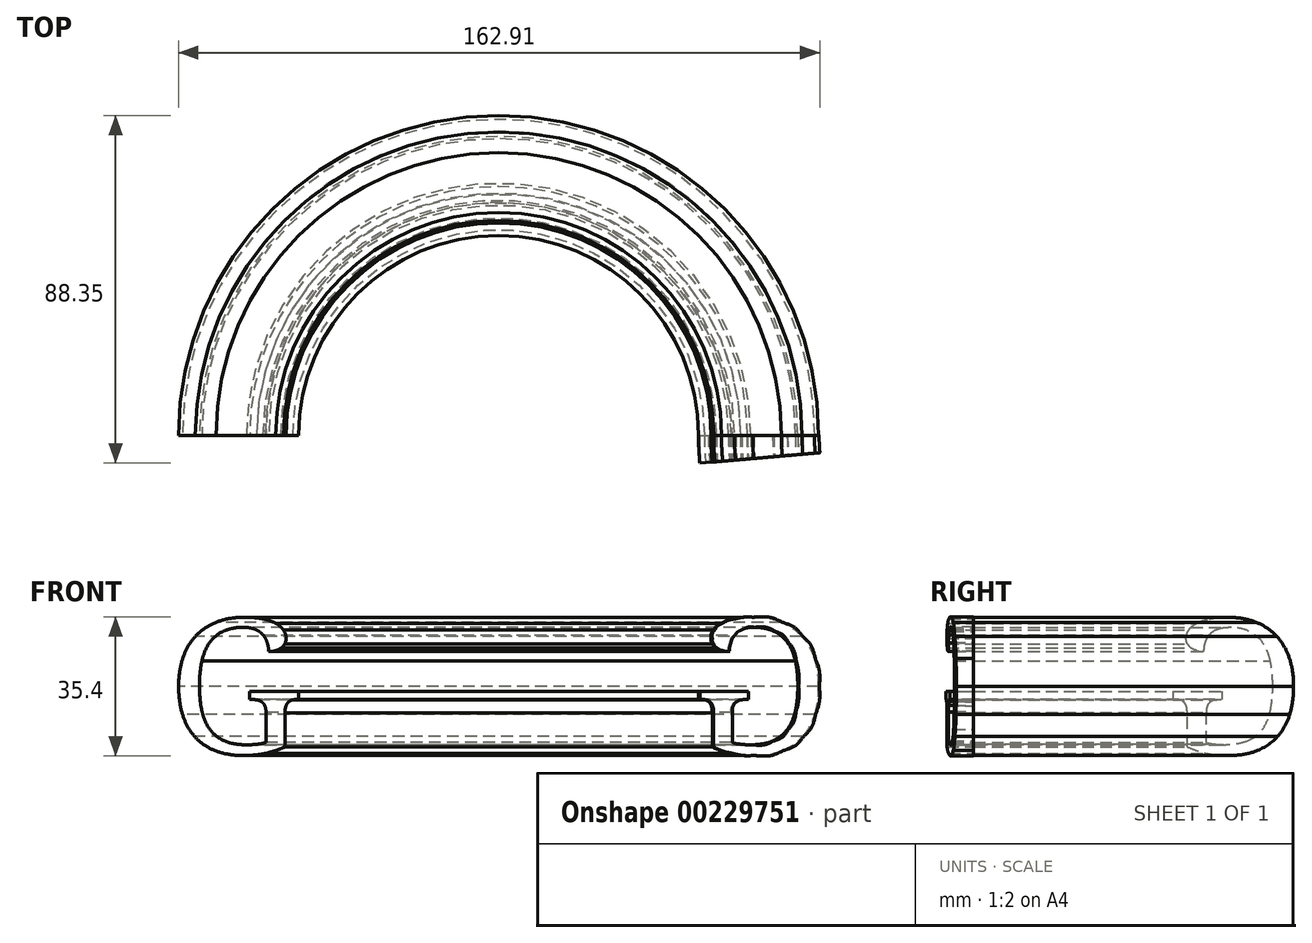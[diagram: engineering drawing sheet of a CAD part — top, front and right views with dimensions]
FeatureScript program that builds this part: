
annotation { "Feature Type Name" : "Feature", "Feature Type Description" : "" }
export const myFeature = defineFeature(function(context is Context, id is Id, definition is map)
    precondition{}
    {
        {
            var Q0;
            Q0=qCreatedBy(makeId("Front.planeOp"),FACE);
            var sketch = newSketch(context, id + "F0", { "sketchPlane" : qUnion([Q0])});
            skLineSegment(sketch, "E0", {"start": v(0, 68.36) * mm, "end": v(0, -21.66) * mm, "construction": true});
            skText(sketch, "E1", { "text": "G", "fontName": "NotoSerif-Regular.ttf"});
            const initialGuessF0  = {"E1": [-0.08404, 0.0145, 1, 0, 0.03445]};
            skSetInitialGuess(sketch, initialGuessF0);
            skSolve(sketch);
        }
        {
            var Q0;
            Q0 = qSketchRegion(id + "F0", true);
            var Q1;
            Q1=sQuery(id+"F0.wireOp",EDGE,"E0");
            revolve(context, id + "F1", {"entities" : qUnion([Q0]), "axis" : qUnion([Q1]), "revolveType" : RevolveType.ONE_DIRECTION, "angle" : 180 * degree});
        }
        {
            var Q0;
            Q0=makeQuery(id+"F1.opRevolve","CAP_FACE",FACE,{"disambiguationData":[OSD([sQuery(id+"F0.wireOp",EDGE,"E1.sketch_text.stroke-0"),sQuery(id+"F0.wireOp",EDGE,"E1.sketch_text.stroke-1"),sQuery(id+"F0.wireOp",EDGE,"E1.sketch_text.stroke-2"),sQuery(id+"F0.wireOp",EDGE,"E1.sketch_text.stroke-3"),sQuery(id+"F0.wireOp",EDGE,"E1.sketch_text.stroke-4"),sQuery(id+"F0.wireOp",EDGE,"E1.sketch_text.stroke-5"),sQuery(id+"F0.wireOp",EDGE,"E1.sketch_text.stroke-6"),sQuery(id+"F0.wireOp",EDGE,"E1.sketch_text.stroke-7"),sQuery(id+"F0.wireOp",EDGE,"E1.sketch_text.stroke-8"),sQuery(id+"F0.wireOp",EDGE,"E1.sketch_text.stroke-9"),sQuery(id+"F0.wireOp",EDGE,"E1.sketch_text.stroke-10"),sQuery(id+"F0.wireOp",EDGE,"E1.sketch_text.stroke-11"),sQuery(id+"F0.wireOp",EDGE,"E1.sketch_text.stroke-12"),sQuery(id+"F0.wireOp",EDGE,"E1.sketch_text.stroke-13"),sQuery(id+"F0.wireOp",EDGE,"E1.sketch_text.stroke-14"),sQuery(id+"F0.wireOp",EDGE,"E1.sketch_text.stroke-15"),sQuery(id+"F0.wireOp",EDGE,"E1.sketch_text.stroke-16"),sQuery(id+"F0.wireOp",EDGE,"E1.sketch_text.stroke-17"),sQuery(id+"F0.wireOp",EDGE,"E1.sketch_text.stroke-18"),sQuery(id+"F0.wireOp",EDGE,"E1.sketch_text.stroke-19"),sQuery(id+"F0.wireOp",EDGE,"E1.sketch_text.stroke-20"),sQuery(id+"F0.wireOp",EDGE,"E1.sketch_text.stroke-21"),sQuery(id+"F0.wireOp",EDGE,"E1.sketch_text.stroke-22"),sQuery(id+"F0.wireOp",EDGE,"E1.sketch_text.stroke-23"),sQuery(id+"F0.wireOp",EDGE,"E1.sketch_text.stroke-24"),sQuery(id+"F0.wireOp",EDGE,"E1.sketch_text.stroke-25"),sQuery(id+"F0.wireOp",EDGE,"E1.sketch_text.stroke-26"),sQuery(id+"F0.wireOp",EDGE,"E1.sketch_text.stroke-27"),sQuery(id+"F0.wireOp",EDGE,"E1.sketch_text.stroke-28"),sQuery(id+"F0.wireOp",EDGE,"E1.sketch_text.stroke-29"),sQuery(id+"F0.wireOp",EDGE,"E1.sketch_text.stroke-30"),sQuery(id+"F0.wireOp",EDGE,"E1.sketch_text.stroke-31"),sQuery(id+"F0.wireOp",EDGE,"E1.sketch_text.stroke-32"),sQuery(id+"F0.wireOp",EDGE,"E1.sketch_text.stroke-33"),sQuery(id+"F0.wireOp",EDGE,"E1.sketch_text.stroke-34"),sQuery(id+"F0.wireOp",EDGE,"E1.sketch_text.stroke-35"),sQuery(id+"F0.wireOp",EDGE,"E1.sketch_text.stroke-36"),sQuery(id+"F0.wireOp",EDGE,"E1.sketch_text.stroke-37"),sQuery(id+"F0.wireOp",EDGE,"E1.sketch_text.stroke-38"),sQuery(id+"F0.wireOp",EDGE,"E1.sketch_text.stroke-39"),sQuery(id+"F0.wireOp",EDGE,"E1.sketch_text.stroke-40"),sQuery(id+"F0.wireOp",EDGE,"E1.sketch_text.stroke-41"),sQuery(id+"F0.wireOp",EDGE,"E1.sketch_text.stroke-42"),sQuery(id+"F0.wireOp",EDGE,"E1.sketch_text.stroke-43"),sQuery(id+"F0.wireOp",EDGE,"E1.sketch_text.stroke-44"),sQuery(id+"F0.wireOp",EDGE,"E1.sketch_text.stroke-45"),sQuery(id+"F0.wireOp",EDGE,"E1.sketch_text.stroke-46")])],"isStart":false});
            cPlane(context, id + "F2", {"entities" : qUnion([Q0]), "cplaneType" : CPlaneType.OFFSET, "offset" : 0 * mm, "width" : 152.4 * mm, "height" : 152.4 * mm});
        }
        {
            var Q0;
            Q0=qCreatedBy(id+"F2.planeOp",FACE);
            var sketch = newSketch(context, id + "F3", { "sketchPlane" : qUnion([Q0])});
            skFitSpline(sketch, "E2.0.0", {"points": [v(59.23, 14.57) * mm, v(61.78, 14.04) * mm, v(64.86, 14.04) * mm]});
            skFitSpline(sketch, "E2.0.1", {"points": [v(64.86, 14.04) * mm, v(69.02, 14.04) * mm, v(72.11, 15.3) * mm]});
            skFitSpline(sketch, "E2.0.2", {"points": [v(72.11, 15.3) * mm, v(75.2, 16.56) * mm, v(77.25, 18.88) * mm]});
            skFitSpline(sketch, "E2.0.3", {"points": [v(77.25, 18.88) * mm, v(79.3, 21.19) * mm, v(80.3, 24.44) * mm]});
            skFitSpline(sketch, "E2.0.4", {"points": [v(80.3, 24.44) * mm, v(81.3, 27.69) * mm, v(81.3, 31.63) * mm]});
            skFitSpline(sketch, "E2.0.5", {"points": [v(81.3, 31.63) * mm, v(81.3, 35.5) * mm, v(80.24, 38.73) * mm]});
            skFitSpline(sketch, "E2.0.6", {"points": [v(80.24, 38.73) * mm, v(79.18, 41.96) * mm, v(77.06, 44.27) * mm]});
            skFitSpline(sketch, "E2.0.7", {"points": [v(77.06, 44.27) * mm, v(74.95, 46.58) * mm, v(71.82, 47.87) * mm]});
            skFitSpline(sketch, "E2.0.8", {"points": [v(71.82, 47.87) * mm, v(68.7, 49.15) * mm, v(64.56, 49.15) * mm]});
            skFitSpline(sketch, "E2.0.9", {"points": [v(64.56, 49.15) * mm, v(61.89, 49.15) * mm, v(59.91, 48.74) * mm]});
            skFitSpline(sketch, "E2.0.10", {"points": [v(59.91, 48.74) * mm, v(57.94, 48.33) * mm, v(56.62, 47.6) * mm]});
            skFitSpline(sketch, "E2.0.11", {"points": [v(56.62, 47.6) * mm, v(55.3, 46.88) * mm, v(54.65, 45.9) * mm]});
            skFitSpline(sketch, "E2.0.12", {"points": [v(54.65, 45.9) * mm, v(54, 44.92) * mm, v(54, 43.78) * mm]});
            skFitSpline(sketch, "E2.0.13", {"points": [v(54, 43.78) * mm, v(54, 43.01) * mm, v(54.35, 42.4) * mm]});
            skFitSpline(sketch, "E2.0.14", {"points": [v(54.35, 42.4) * mm, v(54.7, 41.77) * mm, v(55.3, 41.34) * mm]});
            skFitSpline(sketch, "E2.0.15", {"points": [v(55.3, 41.34) * mm, v(55.89, 40.9) * mm, v(56.7, 40.67) * mm]});
            skFitSpline(sketch, "E2.0.16", {"points": [v(56.7, 40.67) * mm, v(57.5, 40.44) * mm, v(58.43, 40.44) * mm]});
            skFitSpline(sketch, "E2.0.17", {"points": [v(58.43, 40.44) * mm, v(58.43, 41.56) * mm, v(58.76, 42.66) * mm]});
            skFitSpline(sketch, "E2.0.18", {"points": [v(58.76, 42.66) * mm, v(59.08, 43.76) * mm, v(59.83, 44.63) * mm]});
            skFitSpline(sketch, "E2.0.19", {"points": [v(59.83, 44.63) * mm, v(60.58, 45.5) * mm, v(61.8, 46.06) * mm]});
            skFitSpline(sketch, "E2.0.20", {"points": [v(61.8, 46.06) * mm, v(63, 46.6) * mm, v(64.77, 46.6) * mm]});
            skFitSpline(sketch, "E2.0.21", {"points": [v(64.77, 46.6) * mm, v(67.8, 46.6) * mm, v(69.94, 45.61) * mm]});
            skFitSpline(sketch, "E2.0.22", {"points": [v(69.94, 45.61) * mm, v(72.08, 44.62) * mm, v(73.43, 42.72) * mm]});
            skFitSpline(sketch, "E2.0.23", {"points": [v(73.43, 42.72) * mm, v(74.78, 40.81) * mm, v(75.4, 38.02) * mm]});
            skFitSpline(sketch, "E2.0.24", {"points": [v(75.4, 38.02) * mm, v(76, 35.23) * mm, v(76, 31.63) * mm]});
            skFitSpline(sketch, "E2.0.25", {"points": [v(76, 31.63) * mm, v(76, 28.06) * mm, v(75.37, 25.28) * mm]});
            skFitSpline(sketch, "E2.0.26", {"points": [v(75.37, 25.28) * mm, v(74.74, 22.5) * mm, v(73.31, 20.6) * mm]});
            skFitSpline(sketch, "E2.0.27", {"points": [v(73.31, 20.6) * mm, v(71.9, 18.72) * mm, v(69.63, 17.73) * mm]});
            skFitSpline(sketch, "E2.0.28", {"points": [v(69.63, 17.73) * mm, v(67.36, 16.75) * mm, v(64.09, 16.75) * mm]});
            skFitSpline(sketch, "E2.0.29", {"points": [v(64.09, 16.75) * mm, v(62.71, 16.75) * mm, v(61.41, 16.9) * mm]});
            skFitSpline(sketch, "E2.0.30", {"points": [v(61.41, 16.9) * mm, v(60.12, 17.03) * mm, v(59.11, 17.33) * mm]});
            skLineSegment(sketch, "E2.0.31", {"start": v(59.11, 17.33) * mm, "end": v(59.11, 25.04) * mm});
            skFitSpline(sketch, "E2.0.32", {"points": [v(59.11, 25.04) * mm, v(59.11, 26.1) * mm, v(59.43, 26.74) * mm]});
            skFitSpline(sketch, "E2.0.33", {"points": [v(59.43, 26.74) * mm, v(59.74, 27.38) * mm, v(60.28, 27.72) * mm]});
            skFitSpline(sketch, "E2.0.34", {"points": [v(60.28, 27.72) * mm, v(60.82, 28.06) * mm, v(61.53, 28.18) * mm]});
            skFitSpline(sketch, "E2.0.35", {"points": [v(61.53, 28.18) * mm, v(62.24, 28.3) * mm, v(63.04, 28.3) * mm]});
            skLineSegment(sketch, "E2.0.36", {"start": v(63.04, 28.3) * mm, "end": v(63.23, 28.3) * mm});
            skLineSegment(sketch, "E2.0.37", {"start": v(63.23, 28.3) * mm, "end": v(63.23, 30.3) * mm});
            skLineSegment(sketch, "E2.0.38", {"start": v(63.23, 30.3) * mm, "end": v(50.8, 30.3) * mm});
            skLineSegment(sketch, "E2.0.39", {"start": v(50.8, 30.3) * mm, "end": v(50.8, 28.3) * mm});
            skLineSegment(sketch, "E2.0.40", {"start": v(50.8, 28.3) * mm, "end": v(50.98, 28.3) * mm});
            skFitSpline(sketch, "E2.0.41", {"points": [v(50.98, 28.3) * mm, v(51.66, 28.3) * mm, v(52.27, 28.18) * mm]});
            skFitSpline(sketch, "E2.0.42", {"points": [v(52.27, 28.18) * mm, v(52.87, 28.06) * mm, v(53.32, 27.7) * mm]});
            skFitSpline(sketch, "E2.0.43", {"points": [v(53.32, 27.7) * mm, v(53.76, 27.33) * mm, v(54.02, 26.64) * mm]});
            skFitSpline(sketch, "E2.0.44", {"points": [v(54.02, 26.64) * mm, v(54.28, 25.95) * mm, v(54.28, 24.83) * mm]});
            skLineSegment(sketch, "E2.0.45", {"start": v(54.28, 24.83) * mm, "end": v(54.28, 16.23) * mm});
            skFitSpline(sketch, "E2.0.46", {"points": [v(54.28, 16.23) * mm, v(56.69, 15.11) * mm, v(59.23, 14.57) * mm]});
            skLineSegment(sketch, "E3", {"start": v(131.73, 54.14) * mm, "end": v(131.73, 7.6) * mm, "construction": true});
            skLineSegment(sketch, "E4", {"start": v(65.87, 55.13) * mm, "end": v(65.87, 6.47) * mm, "construction": true});
            skSolve(sketch);
        }
        {
            var Q0;
            Q0=makeQuery(id+"F3.imprint","IMPRINT",FACE,{"disambiguationData":[TD([[makeQuery(id+"F3.imprint","IMPRINT",EDGE,{"derivedFrom":sQuery(id+"F3.wireOp",EDGE,"E2.0.0")}),1.0]])]});
            var Q1;
            Q1=sQuery(id+"F3.wireOp",EDGE,"E3");
            revolve(context, id + "F4", {"operationType" : NewBodyOperationType.ADD, "entities" : qUnion([Q0]), "axis" : qUnion([Q1]), "revolveType" : RevolveType.ONE_DIRECTION, "oppositeDirection" : true, "angle" : 5 * degree});
        }
    });
